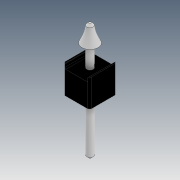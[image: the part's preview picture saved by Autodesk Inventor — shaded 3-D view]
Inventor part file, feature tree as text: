
AUTODESK INVENTOR PART (.ipt)
format: ipt  version: 2020 (Build 240168000, 168)  size: 188,416 bytes
history: native  units: in
note: dims shown in document units (in); Inventor stores cm internally (conversion verified against a paired STEP export)
features: sketch x4, extrude x3, chamfer x3, plane x1, revolve x1, other x1, projected_geometry x1
ambient origin geometry x8: Origin, YZ Plane, XZ Plane, XY Plane, X Axis, Y Axis, Z Axis, Center Point
bodies: Body1 (feature_tree)
feature tree (14):
  extrude  "Extrusion4"  Depth=0.0965in
  extrude  "Extrusion5"  Depth=0.1in
  chamfer  "Chamfer3"  Distance=0.1in
  chamfer  "Chamfer4"  [1 undecoded]
  extrude  "Extrusion6"  Depth=0.0039in TaperAngle=45.0deg
  chamfer  "Chamfer5"  Distance=0.0012in Angle=45.0deg
  plane  "Work Plane1"
  revolve  "Revolution1"  [1 undecoded]
  sketch  "Sketch5"  dims[d33=0.0866in d34=0.0965in]
  sketch  "Sketch6"  dims[d36=0.0059in d37=0.1in d38=0.1in d39=0.0in]
  sketch  "Sketch7"  dims[d40=0.0846in]
  other  "Work Axis1"
  sketch  "Sketch8"  dims[d41=0.0157in d42=0.0in d43=0.0in d44=0.0039in d45=0.0787in d46=45.0deg d47=0.0012in d48=0.0787in d49=45.0deg d50=0.0236in d51=0.1417in d52=0.2835in d53=0.0in d54=0.0in d55=0.0079in d56=0.0787in d57=45.0deg d58=90.0deg d59=0.062in d61=0.0295in d62=180.0deg]
  projected_geometry  "Projected Loop1"
note: 2 required parameter values undecoded (feature->parameter linkage not recoverable at this tier; creation-order binding heuristic only, values carry confidence <= 0.55)